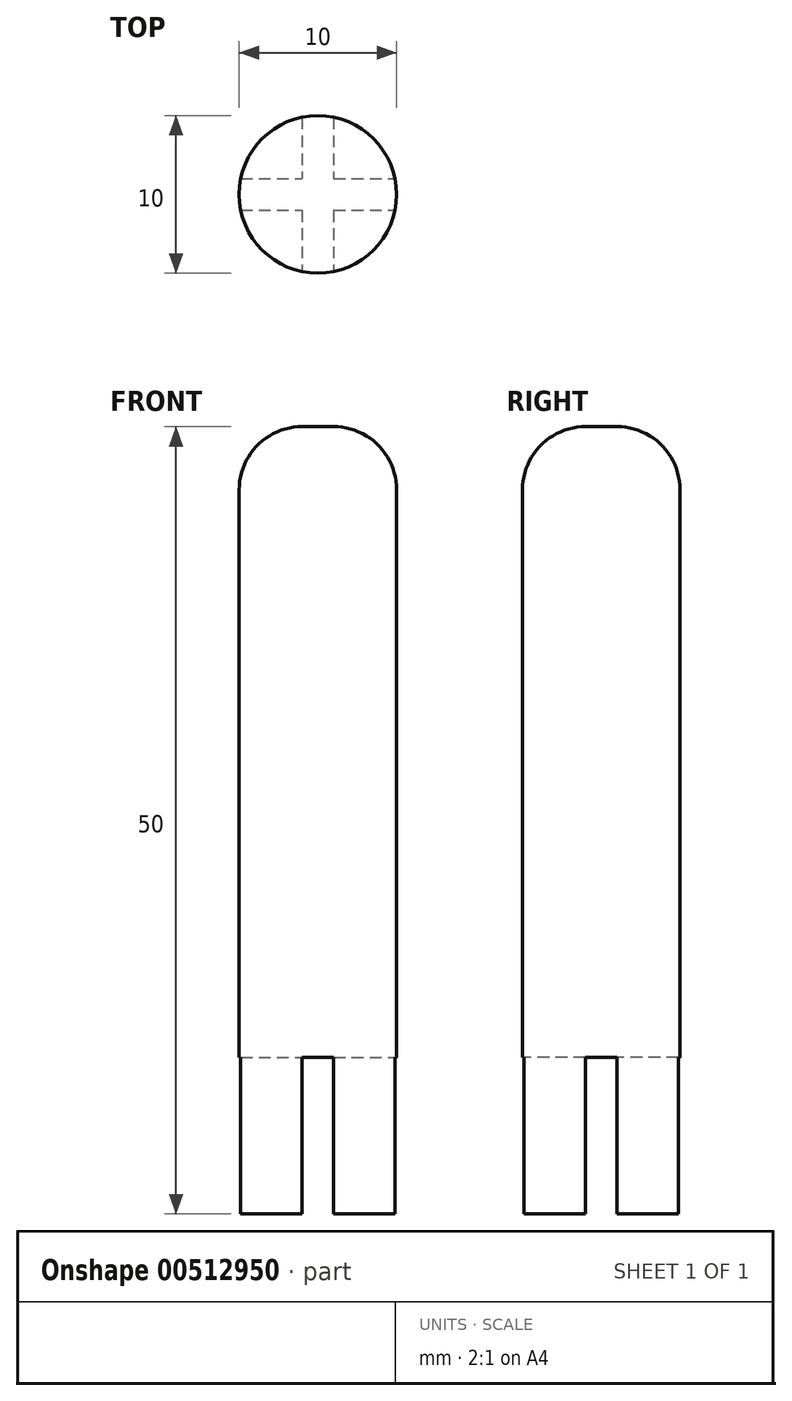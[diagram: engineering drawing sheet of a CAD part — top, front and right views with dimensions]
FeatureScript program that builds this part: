
annotation { "Feature Type Name" : "Feature", "Feature Type Description" : "" }
export const myFeature = defineFeature(function(context is Context, id is Id, definition is map)
    precondition{}
    {
        {
            var Q0;
            Q0=qCreatedBy(makeId("Right.planeOp"),FACE);
            var sketch = newSketch(context, id + "F0", { "sketchPlane" : qUnion([Q0])});
            skLineSegment(sketch, "E0.bottom", {"start": v(0, 40.06) * mm, "end": v(-1, 40.06) * mm});
            skLineSegment(sketch, "E0.top", {"start": v(0, -9.94) * mm, "end": v(-5, -9.94) * mm});
            skLineSegment(sketch, "E0.left", {"start": v(0, 40.06) * mm, "end": v(0, -9.94) * mm});
            skLineSegment(sketch, "E0.right", {"start": v(-5, 36.06) * mm, "end": v(-5, -9.94) * mm});
            skPoint(sketch, "E1.visualSharp", {"position": v(-5, 40.06) * mm});
            skArc(sketch, "E1.filletArc", {"start": v(-1, 40.06) * mm, "mid": v(-3.83, 38.89) * mm, "end": v(-5, 36.06) * mm});
            skSolve(sketch);
        }
        {
            var Q0;
            Q0 = qSketchRegion(id + "F0", true);
            var Q1;
            Q1=sQuery(id+"F0.wireOp",EDGE,"E0.left");
            revolve(context, id + "F1", {"entities" : qUnion([Q0]), "axis" : qUnion([Q1]), "revolveType" : RevolveType.FULL});
        }
        {
            var Q0;
            Q0=qCreatedBy(makeId("Top.planeOp"),FACE);
            var sketch = newSketch(context, id + "F2", { "sketchPlane" : qUnion([Q0])});
            skLineSegment(sketch, "E2.bottom", {"start": v(-5, 1) * mm, "end": v(5, 1) * mm});
            skLineSegment(sketch, "E2.top", {"start": v(-5, -1) * mm, "end": v(5, -1) * mm});
            skLineSegment(sketch, "E2.left", {"start": v(-5, 1) * mm, "end": v(-5, -1) * mm});
            skLineSegment(sketch, "E2.right", {"start": v(5, 1) * mm, "end": v(5, -1) * mm});
            skSolve(sketch);
        }
        {
            var Q0;
            Q0 = qSketchRegion(id + "F2", true);
            extrude(context, id + "F3", {"entities" : qUnion([Q0]), "operationType" : NewBodyOperationType.REMOVE, "oppositeDirection" : true, "depth" : 25 * mm});
        }
        {
            var Q0;
            Q0=qCreatedBy(makeId("Top.planeOp"),FACE);
            var sketch = newSketch(context, id + "F4", { "sketchPlane" : qUnion([Q0])});
            skPoint(sketch, "E3.bottom.start.orphan", {"position": v(0, 11.37) * mm});
            skLineSegment(sketch, "E4.bottom", {"start": v(-1, 5) * mm, "end": v(1, 5) * mm});
            skLineSegment(sketch, "E4.top", {"start": v(-1, -5) * mm, "end": v(1, -5) * mm});
            skLineSegment(sketch, "E4.left", {"start": v(-1, 5) * mm, "end": v(-1, -5) * mm});
            skLineSegment(sketch, "E4.right", {"start": v(1, 5) * mm, "end": v(1, -5) * mm});
            skSolve(sketch);
        }
        {
            var Q0;
            Q0 = qSketchRegion(id + "F4", true);
            extrude(context, id + "F5", {"entities" : qUnion([Q0]), "operationType" : NewBodyOperationType.REMOVE, "oppositeDirection" : true, "depth" : 25 * mm});
        }
    });
